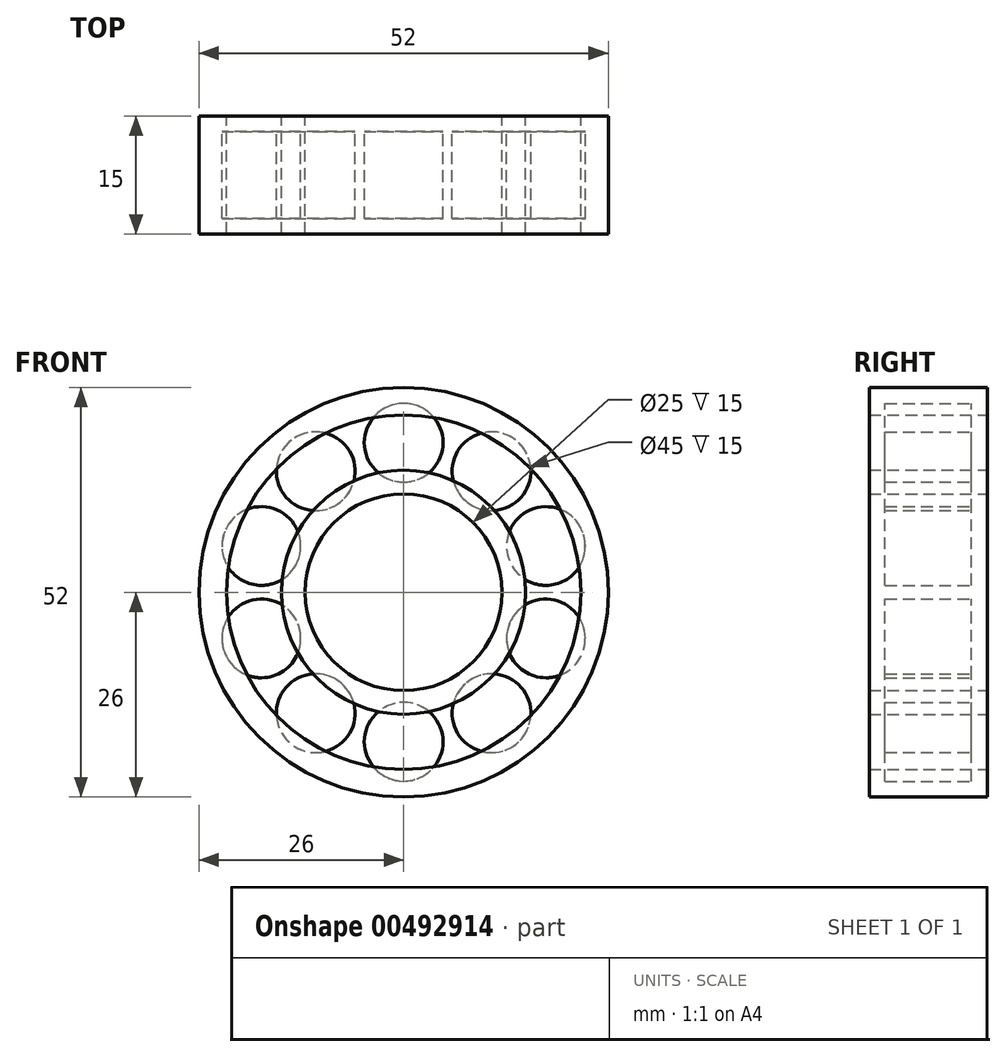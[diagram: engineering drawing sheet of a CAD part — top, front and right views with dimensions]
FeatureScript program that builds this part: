
annotation { "Feature Type Name" : "Feature", "Feature Type Description" : "" }
export const myFeature = defineFeature(function(context is Context, id is Id, definition is map)
    precondition{}
    {
        {
            var Q0;
            Q0=qCreatedBy(makeId("Front.planeOp"),FACE);
            var sketch = newSketch(context, id + "F0", { "sketchPlane" : qUnion([Q0])});
            skCircle(sketch, "E0", {"center": v(0, 0) * mm, "radius": 12.5 * mm});
            skCircle(sketch, "E1", {"center": v(0, 0) * mm, "radius": 15.5 * mm});
            skCircle(sketch, "E2", {"center": v(0, 0) * mm, "radius": 22.5 * mm});
            skCircle(sketch, "E3", {"center": v(0, 0) * mm, "radius": 26 * mm});
            skSolve(sketch);
        }
        {
            var Q0;
            Q0=makeQuery(id+"F0.imprint","IMPRINT",FACE,{"disambiguationData":[TD([[makeQuery(id+"F0.imprint","IMPRINT",EDGE,{"derivedFrom":sQuery(id+"F0.wireOp",EDGE,"E2")}),-1.0]])]});
            var Q1;
            Q1=makeQuery(id+"F0.imprint","IMPRINT",FACE,{"disambiguationData":[TD([[makeQuery(id+"F0.imprint","IMPRINT",EDGE,{"derivedFrom":sQuery(id+"F0.wireOp",EDGE,"E0")}),-1.0]])]});
            extrude(context, id + "F1", {"entities" : qUnion([Q0, Q1]), "depth" : 15 * mm, "offsetDistance" : 25 * mm, "symmetric" : true});
        }
        {
            var Q0;
            Q0=qCreatedBy(makeId("Front.planeOp"),FACE);
            var sketch = newSketch(context, id + "F2", { "sketchPlane" : qUnion([Q0])});
            skCircle(sketch, "E4", {"center": v(0, 0) * mm, "radius": 19 * mm, "construction": true});
            skCircle(sketch, "E5", {"center": v(0, 19) * mm, "radius": 5 * mm});
            skCircle(sketch, "E6.1.0", {"center": v(-11.17, 15.37) * mm, "radius": 5 * mm});
            skCircle(sketch, "E6.2.0", {"center": v(-18.07, 5.87) * mm, "radius": 5 * mm});
            skCircle(sketch, "E7.1.3.0", {"center": v(-18.07, -5.87) * mm, "radius": 5 * mm});
            skCircle(sketch, "E7.1.4.0", {"center": v(-11.17, -15.37) * mm, "radius": 5 * mm});
            skCircle(sketch, "E7.1.5.0", {"center": v(0, -19) * mm, "radius": 5 * mm});
            skCircle(sketch, "E7.1.6.0", {"center": v(11.17, -15.37) * mm, "radius": 5 * mm});
            skCircle(sketch, "E7.1.7.0", {"center": v(18.07, -5.87) * mm, "radius": 5 * mm});
            skCircle(sketch, "E7.1.8.0", {"center": v(18.07, 5.87) * mm, "radius": 5 * mm});
            skCircle(sketch, "E7.1.9.0", {"center": v(11.17, 15.37) * mm, "radius": 5 * mm});
            skSolve(sketch);
        }
        {
            var Q0;
            Q0 = qSketchRegion(id + "F2", true);
            extrude(context, id + "F3", {"entities" : qUnion([Q0]), "depth" : 11 * mm, "offsetDistance" : 25 * mm, "symmetric" : true});
        }
    });
